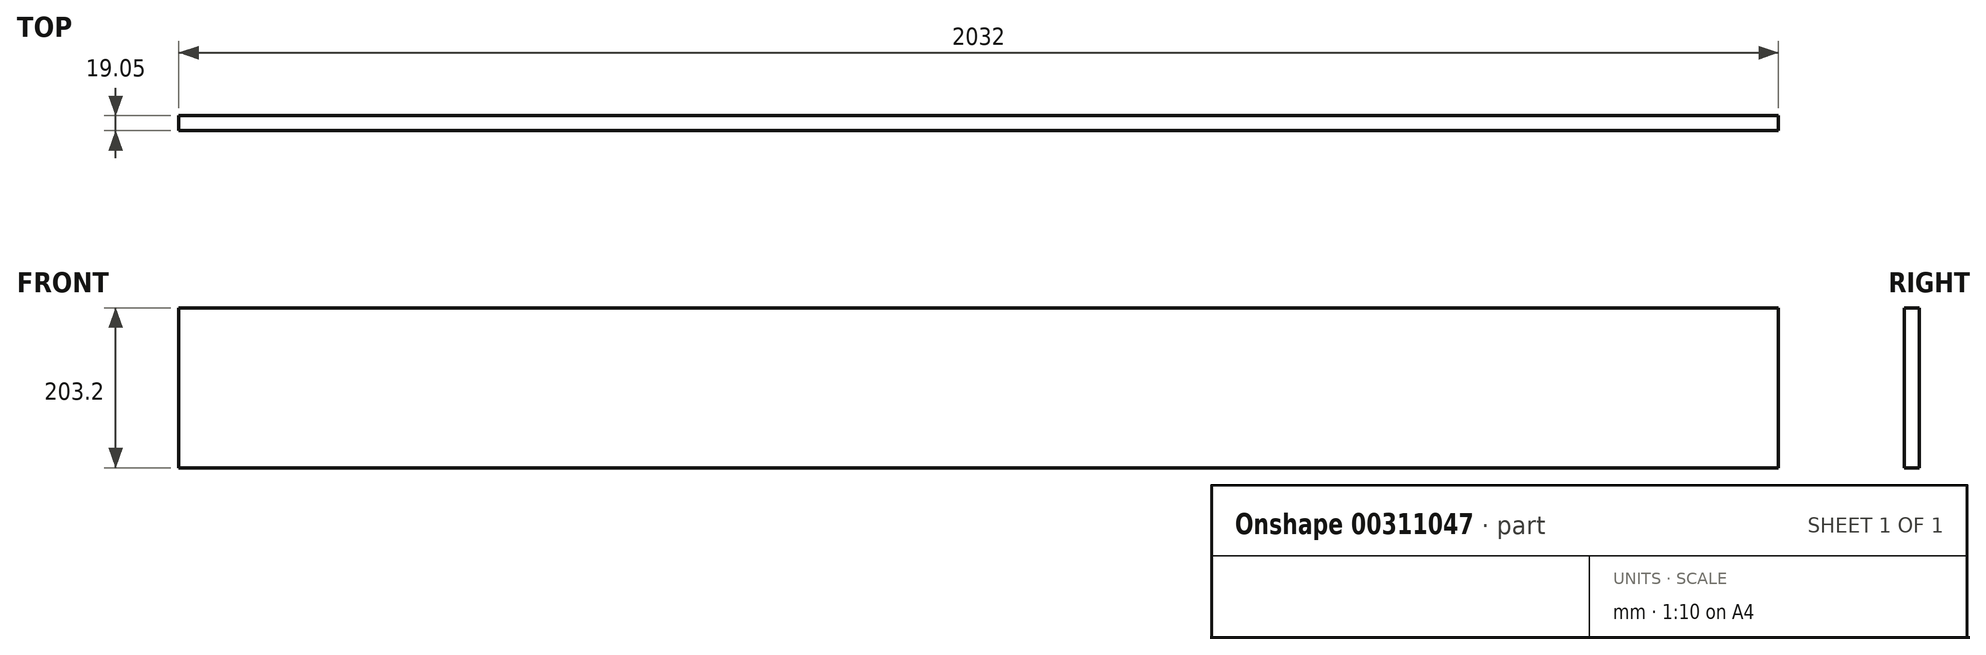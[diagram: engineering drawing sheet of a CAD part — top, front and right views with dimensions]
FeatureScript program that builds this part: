
annotation { "Feature Type Name" : "Feature", "Feature Type Description" : "" }
export const myFeature = defineFeature(function(context is Context, id is Id, definition is map)
    precondition{}
    {
        {
            var Q0;
            Q0=qCreatedBy(makeId("Front.planeOp"),FACE);
            var sketch = newSketch(context, id + "F0", { "sketchPlane" : qUnion([Q0])});
            skLineSegment(sketch, "E0.bottom", {"start": v(-1715, 218.94) * mm, "end": v(317, 218.94) * mm});
            skLineSegment(sketch, "E0.top", {"start": v(-1715, 15.74) * mm, "end": v(317, 15.74) * mm});
            skLineSegment(sketch, "E0.left", {"start": v(-1715, 218.94) * mm, "end": v(-1715, 15.74) * mm});
            skLineSegment(sketch, "E0.right", {"start": v(317, 218.94) * mm, "end": v(317, 15.74) * mm});
            skSolve(sketch);
        }
        {
            var Q0;
            Q0=makeQuery(id+"F0.imprint","IMPRINT",FACE,{"disambiguationData":[TD([[makeQuery(id+"F0.imprint","IMPRINT",EDGE,{"derivedFrom":sQuery(id+"F0.wireOp",EDGE,"E0.bottom")}),-1.0]])]});
            extrude(context, id + "F1", {"entities" : qUnion([Q0]), "depth" : 19.05 * mm});
        }
    });
